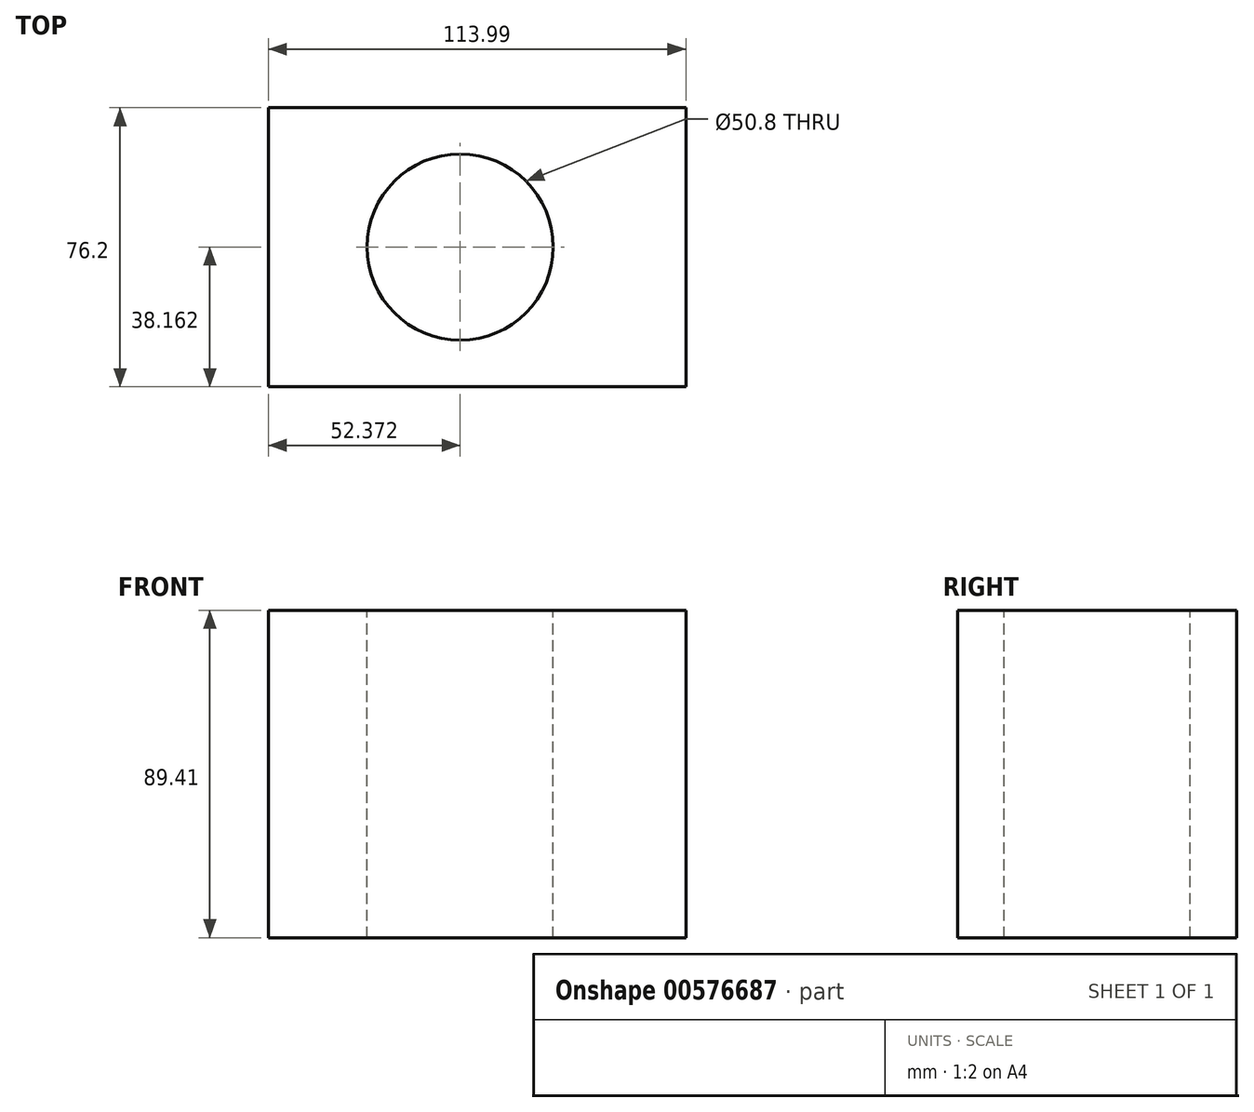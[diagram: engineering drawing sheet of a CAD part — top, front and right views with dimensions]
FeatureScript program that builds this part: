
annotation { "Feature Type Name" : "Feature", "Feature Type Description" : "" }
export const myFeature = defineFeature(function(context is Context, id is Id, definition is map)
    precondition{}
    {
        {
            var Q0;
            Q0=qCreatedBy(makeId("Front.planeOp"),FACE);
            var sketch = newSketch(context, id + "F0", { "sketchPlane" : qUnion([Q0])});
            skLineSegment(sketch, "E0.bottom", {"start": v(-40.4, -38.76) * mm, "end": v(73.59, -38.76) * mm});
            skLineSegment(sketch, "E0.top", {"start": v(-40.4, 50.65) * mm, "end": v(73.59, 50.65) * mm});
            skLineSegment(sketch, "E0.left", {"start": v(-40.4, -38.76) * mm, "end": v(-40.4, 50.65) * mm});
            skLineSegment(sketch, "E0.right", {"start": v(73.59, -38.76) * mm, "end": v(73.59, 50.65) * mm});
            skSolve(sketch);
        }
        {
            var Q0;
            Q0=makeQuery(id+"F0.imprint","IMPRINT",FACE,{"disambiguationData":[TD([[makeQuery(id+"F0.imprint","IMPRINT",EDGE,{"derivedFrom":sQuery(id+"F0.wireOp",EDGE,"E0.bottom")}),1.0]])]});
            extrude(context, id + "F1", {"entities" : qUnion([Q0]), "depth" : 76.2 * mm, "offsetDistance" : 25.4 * mm});
        }
        {
            var Q0;
            Q0=makeQuery(id+"F1.opExtrude","SWEPT_FACE",FACE,{"disambiguationData":[OSD([sQuery(id+"F0.wireOp",EDGE,"E0.top")])]});
            var sketch = newSketch(context, id + "F2", { "sketchPlane" : qUnion([Q0])});
            skPoint(sketch, "E1", {"position": v(11.97, -38.04) * mm});
            skCircle(sketch, "E2", {"center": v(11.97, -38.04) * mm, "radius": 20.02 * mm});
            skSolve(sketch);
        }
        {
            var Q0;
            Q0=sQuery(id+"F2.wireOp",VERTEX,"E1");
            var Q1;
            Q1=makeQuery(id+"F1.opExtrude","SWEPT_BODY",BODY,{"disambiguationData":[OSD([sQuery(id+"F0.wireOp",EDGE,"E0.bottom"),sQuery(id+"F0.wireOp",EDGE,"E0.top"),sQuery(id+"F0.wireOp",EDGE,"E0.left"),sQuery(id+"F0.wireOp",EDGE,"E0.right")])]});
            hole(context, id + "F3", {"style" : HoleStyle.SIMPLE, "endStyle" : HoleEndStyle.THROUGH, "holeDiameter" : 50.8 * mm, "isTappedThrough" : true, "tappedDepth" : 12.7 * mm, "tapClearance" : 3, "locations" : qUnion([Q0]), "scope" : qUnion([Q1])});
        }
    });
